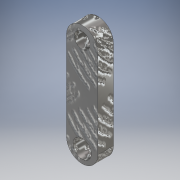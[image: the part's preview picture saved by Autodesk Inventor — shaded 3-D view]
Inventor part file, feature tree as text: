
AUTODESK INVENTOR PART (.ipt)
format: ipt  version: 2017 (Build 210142000, 142)  size: 133,120 bytes
history: native  units: mm
features: fillet x2, extrude x1, sketch x1
ambient origin geometry x8: Origin, YZ Plane, XZ Plane, XY Plane, X Axis, Y Axis, Z Axis, Center Point
bodies: Solid1 (feature_tree)
feature tree (4):
  extrude  "Extrusion1"  Depth=3.0mm
  fillet  "Fillet1"  Radius=6.0mm
  fillet  "Fillet2"  Radius=3.0mm
  sketch  "Sketch1"  dims[d0=6.0mm d1=23.0mm d2=6.0mm d4=3.0mm d5=3.5mm d6=2.5mm d7=2.5mm d8=3.0mm d9=0.0mm d10=3.0mm d11=3.0mm]
